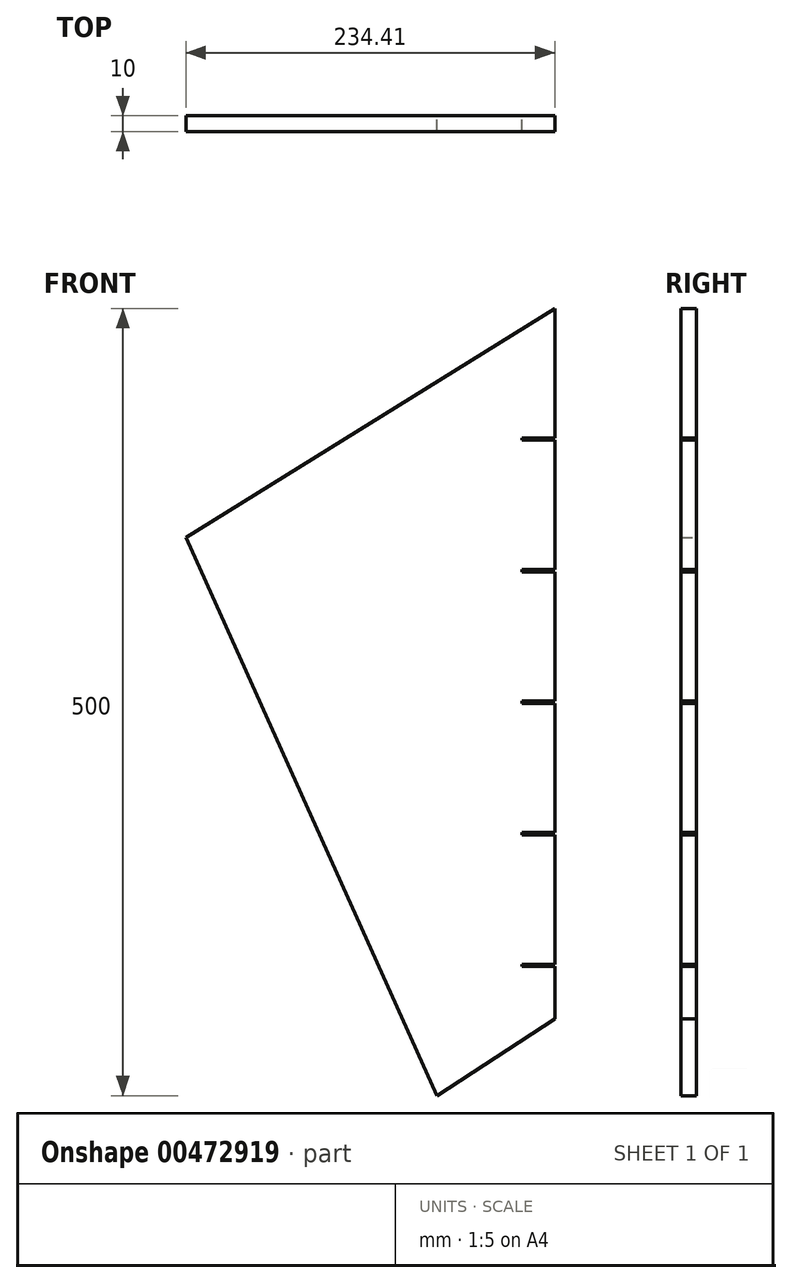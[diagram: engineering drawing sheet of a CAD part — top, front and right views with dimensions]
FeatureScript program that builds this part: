
annotation { "Feature Type Name" : "Feature", "Feature Type Description" : "" }
export const myFeature = defineFeature(function(context is Context, id is Id, definition is map)
    precondition{}
    {
        {
            var Q0;
            Q0=qCreatedBy(makeId("Front.planeOp"),FACE);
            var sketch = newSketch(context, id + "F0", { "sketchPlane" : qUnion([Q0])});
            skLineSegment(sketch, "E0", {"start": v(0, 48.96) * mm, "end": v(0, 82.08) * mm});
            skLineSegment(sketch, "E1.bottom", {"start": v(0, 82.08) * mm, "end": v(-21, 82.08) * mm});
            skLineSegment(sketch, "E1.top", {"start": v(0, 83.58) * mm, "end": v(-21, 83.58) * mm});
            skLineSegment(sketch, "E1.right", {"start": v(-21, 82.08) * mm, "end": v(-21, 83.58) * mm});
            skLineSegment(sketch, "E2.bottom", {"start": v(0, 165.67) * mm, "end": v(-21, 165.67) * mm});
            skLineSegment(sketch, "E2.top", {"start": v(0, 167.17) * mm, "end": v(-21, 167.17) * mm});
            skLineSegment(sketch, "E2.right", {"start": v(-21, 165.67) * mm, "end": v(-21, 167.17) * mm});
            skLineSegment(sketch, "E3.bottom", {"start": v(0, 249.25) * mm, "end": v(-21, 249.25) * mm});
            skLineSegment(sketch, "E3.top", {"start": v(0, 250.75) * mm, "end": v(-21, 250.75) * mm});
            skLineSegment(sketch, "E3.right", {"start": v(-21, 249.25) * mm, "end": v(-21, 250.75) * mm});
            skLineSegment(sketch, "E4.bottom", {"start": v(0, 332.83) * mm, "end": v(-21, 332.83) * mm});
            skLineSegment(sketch, "E4.top", {"start": v(0, 334.33) * mm, "end": v(-21, 334.33) * mm});
            skLineSegment(sketch, "E4.right", {"start": v(-21, 332.83) * mm, "end": v(-21, 334.33) * mm});
            skLineSegment(sketch, "E5.bottom", {"start": v(0, 416.42) * mm, "end": v(-21, 416.42) * mm});
            skLineSegment(sketch, "E5.top", {"start": v(0, 417.92) * mm, "end": v(-21, 417.92) * mm});
            skLineSegment(sketch, "E5.right", {"start": v(-21, 416.42) * mm, "end": v(-21, 417.92) * mm});
            skLineSegment(sketch, "E6", {"start": v(0, 500) * mm, "end": v(-234.4, 354.55) * mm});
            skLineSegment(sketch, "E7", {"start": v(-234.4, 354.55) * mm, "end": v(-75, 0) * mm});
            skLineSegment(sketch, "E8.trimOffspring", {"start": v(0, 417.92) * mm, "end": v(0, 500) * mm});
            skLineSegment(sketch, "E9.trimOffspring", {"start": v(0, 334.33) * mm, "end": v(0, 416.42) * mm});
            skLineSegment(sketch, "E10.trimOffspring", {"start": v(0, 250.75) * mm, "end": v(0, 332.83) * mm});
            skLineSegment(sketch, "E11.trimOffspring", {"start": v(0, 167.17) * mm, "end": v(0, 249.25) * mm});
            skLineSegment(sketch, "E12.trimOffspring", {"start": v(0, 83.58) * mm, "end": v(0, 165.67) * mm});
            skLineSegment(sketch, "E13", {"start": v(-75, 0) * mm, "end": v(0, 48.96) * mm});
            skPoint(sketch, "E14.start.orphan", {"position": v(0, 0) * mm});
            skSolve(sketch);
        }
        {
            var Q0;
            Q0=makeQuery(id+"F0.imprint","IMPRINT",FACE,{"disambiguationData":[TD([[makeQuery(id+"F0.imprint","IMPRINT",EDGE,{"derivedFrom":sQuery(id+"F0.wireOp",EDGE,"E0")}),1.0]])]});
            extrude(context, id + "F1", {"entities" : qUnion([Q0]), "depth" : 10 * mm});
        }
    });
